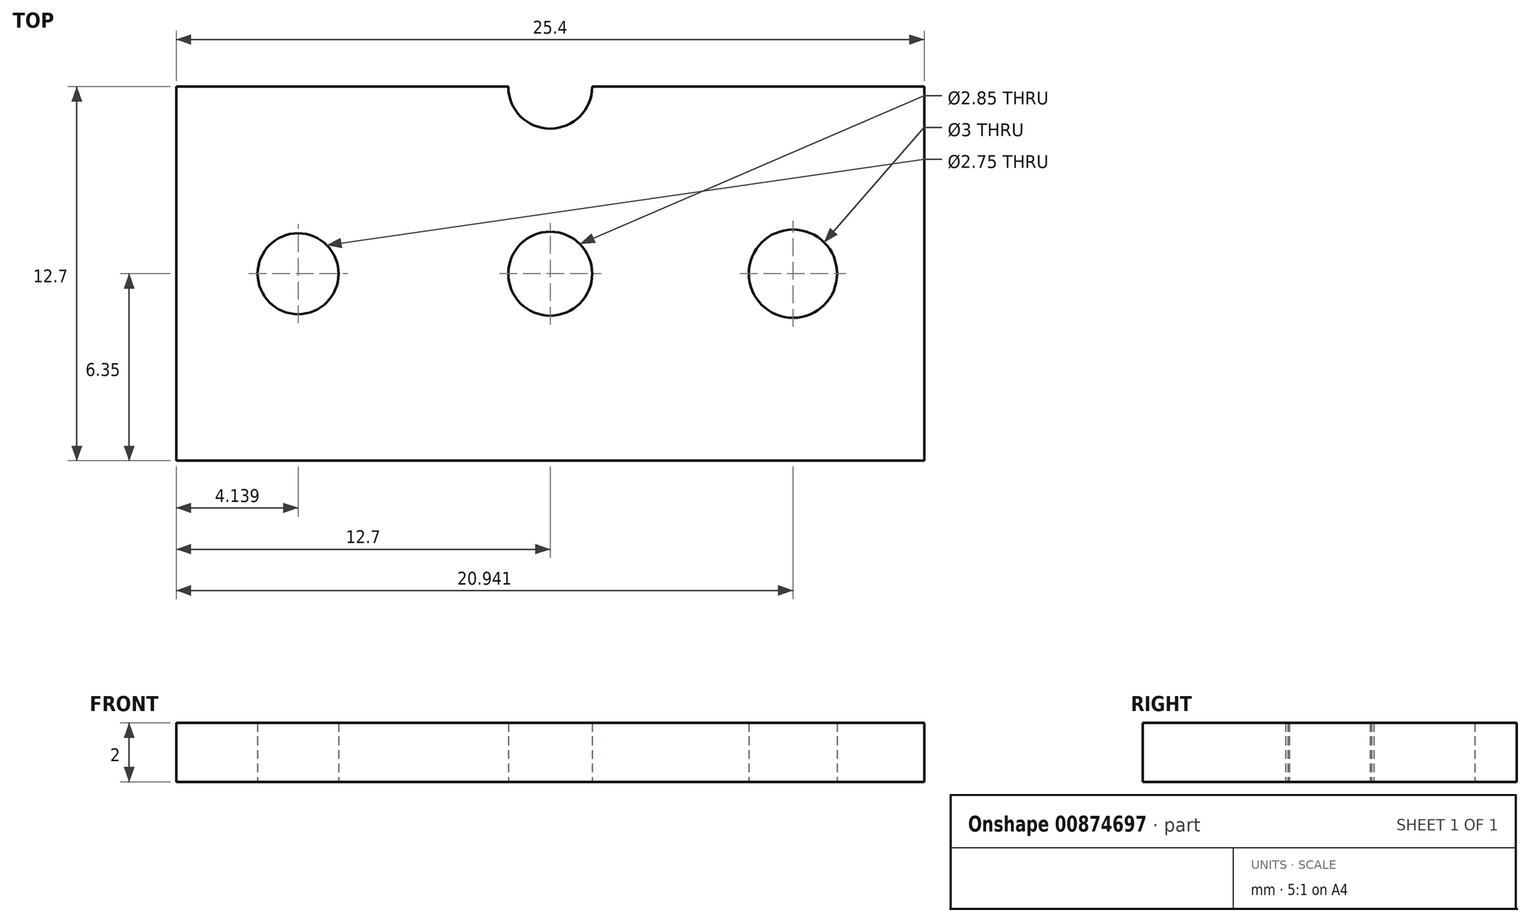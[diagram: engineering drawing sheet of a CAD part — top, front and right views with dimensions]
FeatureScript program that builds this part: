
annotation { "Feature Type Name" : "Feature", "Feature Type Description" : "" }
export const myFeature = defineFeature(function(context is Context, id is Id, definition is map)
    precondition{}
    {
        {
            var Q0;
            Q0=qCreatedBy(makeId("Top.planeOp"),FACE);
            var sketch = newSketch(context, id + "F0", { "sketchPlane" : qUnion([Q0])});
            skLineSegment(sketch, "E0.bottom", {"start": v(12.7, 6.35) * mm, "end": v(-12.7, 6.35) * mm});
            skLineSegment(sketch, "E0.top", {"start": v(12.7, -6.35) * mm, "end": v(-12.7, -6.35) * mm});
            skLineSegment(sketch, "E0.left", {"start": v(12.7, 6.35) * mm, "end": v(12.7, -6.35) * mm});
            skLineSegment(sketch, "E0.right", {"start": v(-12.7, 6.35) * mm, "end": v(-12.7, -6.35) * mm});
            skPoint(sketch, "E0.middle", {"position": v(0, 0) * mm});
            skPoint(sketch, "E1", {"position": v(-8.56, 0) * mm});
            skPoint(sketch, "E2", {"position": v(8.24, 0) * mm});
            skPoint(sketch, "E3", {"position": v(0, 6.35) * mm});
            skSolve(sketch);
        }
        {
            var Q0;
            Q0 = qSketchRegion(id + "F0", true);
            extrude(context, id + "F1", {"entities" : qUnion([Q0]), "depth" : 2 * mm, "offsetDistance" : 25 * mm});
        }
        {
            var Q0;
            Q0=sQuery(id+"F0.wireOp",VERTEX,"E0.middle");
            var Q1;
            Q1=sQuery(id+"F0.wireOp",VERTEX,"E3");
            var Q2;
            Q2=makeQuery(id+"F1.opExtrude","SWEPT_BODY",BODY,{"disambiguationData":[OSD([sQuery(id+"F0.wireOp",EDGE,"E0.bottom"),sQuery(id+"F0.wireOp",EDGE,"E0.top"),sQuery(id+"F0.wireOp",EDGE,"E0.left"),sQuery(id+"F0.wireOp",EDGE,"E0.right")])]});
            hole(context, id + "F2", {"style" : HoleStyle.SIMPLE, "endStyle" : HoleEndStyle.THROUGH, "oppositeDirection" : true, "holeDiameter" : 2.85 * mm, "majorDiameter" : 5 * mm, "isTappedThrough" : true, "tappedDepth" : 12 * mm, "tapClearance" : 3, "locations" : qUnion([Q0, Q1]), "scope" : qUnion([Q2])});
        }
        {
            var Q0;
            Q0=sQuery(id+"F0.wireOp",VERTEX,"E2");
            var Q1;
            Q1=makeQuery(id+"F1.opExtrude","SWEPT_BODY",BODY,{"disambiguationData":[OSD([sQuery(id+"F0.wireOp",EDGE,"E0.bottom"),sQuery(id+"F0.wireOp",EDGE,"E0.top"),sQuery(id+"F0.wireOp",EDGE,"E0.left"),sQuery(id+"F0.wireOp",EDGE,"E0.right")])]});
            hole(context, id + "F3", {"style" : HoleStyle.SIMPLE, "endStyle" : HoleEndStyle.THROUGH, "oppositeDirection" : true, "holeDiameter" : 3 * mm, "majorDiameter" : 5 * mm, "isTappedThrough" : true, "tappedDepth" : 12 * mm, "tapClearance" : 3, "locations" : qUnion([Q0]), "scope" : qUnion([Q1])});
        }
        {
            var Q0;
            Q0=sQuery(id+"F0.wireOp",VERTEX,"E1");
            var Q1;
            Q1=makeQuery(id+"F1.opExtrude","SWEPT_BODY",BODY,{"disambiguationData":[OSD([sQuery(id+"F0.wireOp",EDGE,"E0.bottom"),sQuery(id+"F0.wireOp",EDGE,"E0.top"),sQuery(id+"F0.wireOp",EDGE,"E0.left"),sQuery(id+"F0.wireOp",EDGE,"E0.right")])]});
            hole(context, id + "F4", {"style" : HoleStyle.SIMPLE, "endStyle" : HoleEndStyle.THROUGH, "oppositeDirection" : true, "holeDiameter" : 2.75 * mm, "majorDiameter" : 5 * mm, "isTappedThrough" : true, "tappedDepth" : 12 * mm, "tapClearance" : 3, "locations" : qUnion([Q0]), "scope" : qUnion([Q1])});
        }
    });
